# Revit family: Gira_206800
name_source: partatom
category: Electrical Fixtures
revit_build: Autodesk Revit 2017 (Build: 20160225_1515(x64)
units: mm (PartAtom-declared; Revit-internal decimal feet)

## family parameters
Cut with Voids When Loaded = No
Host = Face
Maintain Annotation Orientation = Yes
Part Type = Normal
Room Calculation Point = No
Round Connector Dimension = Use Diameter
Shared = No

## types (1)
- Gira Control 19 Client 2 Electronics
    Available = No
    BIM (1) = https://media.stage.bim.site Client.rfa?public/gira/36a6b08/GiraHomeServer_GC19 Client.rfa
    Bus connection included = Yes
    Bus system KNX = Yes
    Bus system KNX radio = No
    Bus system LON = No
    Bus system Powernet = No
    Bus system radio frequent = No
    Category = Multi operating device for bus system
    Central functional unit for senders/actuators = Yes
    Data sheet (1) = https://katalog.gira.de
    Default Elevation = 1219 mm
    Degree of protection (IP) = IP20
    Description = Gira Control 19 Client 2 Elec.,Gira Control 19 Client 2,,,The Gira Control 19 Client is a display and operating unit for connection to the Gira HomeServer or Gira FacilityServer. The device is PC-based and has a TFT touch screen with 47 cm (19) screen diagonal.,,Features:,- Visualisation and operation of building system technology functions in conjunction with the Gira HomeServer and or the Gira FacilityServer.,- Display of e-mails.,- Playback of acoustic signals.,- Suitable for door communication systems as a home station (via DCS-IP gateway).,Device features:,- PC with touch screen.,- Integrated power supply unit.,- Integrated speaker.,- Integrated microphone.,,Software:,Microsoft operating system(r) Windows(r) embedded Standard 7.: ,,Notes :,- Can also be installed in existing Gira Pro-face ServerClient 15 device boxes.,- Suitable for indoor use only.,- Areas of application: ,  - Operation in stationary environment..,  - Operation only in environmental conditions that meet the specifications regarding temperature, humidity, dust, vibrations etc...
    GTIN = 4010337022367
    HAN = 206800
    HeinzeBIM = https://bimportal.heinze.de
    Manufacturer = Gira
    Manufacturer URL = https://www.gira.de
    Material = Other
    Material quality = Other
    Mounting method = Flush mounted (plaster)
    Name = Gira Control 19 Client 2 Electronics
    Other bus systems = None
    Radio frequent bidirectional = No
    Surface finishing = Not applicable
    Surface protection = Other
    Transparent = No
    URL = http://katalog.gira.de
    With display = Yes

## geometry (parser evidence)
native form markers: Sweep x6
no freeform markers — native parametric forms only
